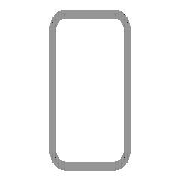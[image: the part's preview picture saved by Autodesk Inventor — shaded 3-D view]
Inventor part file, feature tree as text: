
AUTODESK INVENTOR PART (.ipt)
format: ipt  version: 2025.1 (Build 291241020, 241B)  size: 143,360 bytes
history: native  units: mm (DEFAULTED — no unit token found)
features: other x4, plane x2, split x1, sketch x1
ambient origin geometry x8: Origin, YZ Plane, XZ Plane, XY Plane, X Axis, Y Axis, Z Axis, Center Point
bodies: Solid1 (feature_tree), Body (feature_tree)
feature tree (8):
  parser-record x1  (decoder bookkeeping rows leaked as tree rows — omitted from the tree; the rows remain in map.json)
  other  "Driven Length"
  other  "Start Plane"
  other  "End Plane"
  plane  "Work Plane4"
  split  "Split1"
  sketch  "Sketch3"  dims[d3=154.948996mm d4=0.0mm d7=6.0mm d9=40.0mm d11=80.0mm d12=3.0mm d13=80.0mm d14=234.948996mm d15=20.0mm d16=40.0mm d17=90.0deg d18=154.948996mm]
  plane  "Work Plane3"
